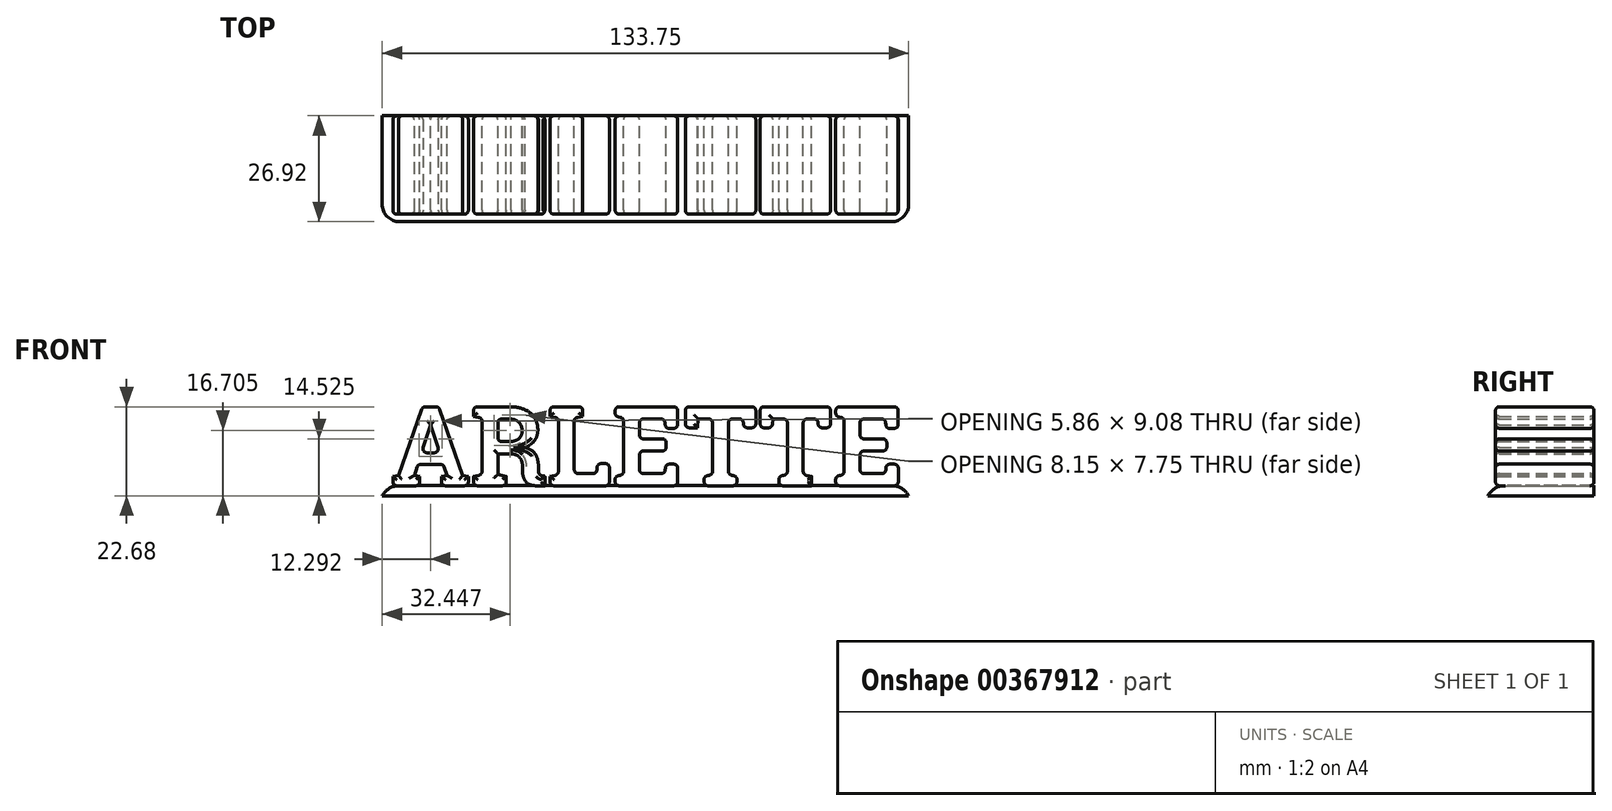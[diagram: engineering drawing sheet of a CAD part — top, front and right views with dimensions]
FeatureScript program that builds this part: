
annotation { "Feature Type Name" : "Feature", "Feature Type Description" : "" }
export const myFeature = defineFeature(function(context is Context, id is Id, definition is map)
    precondition{}
    {
        {
            var Q0;
            Q0=qCreatedBy(makeId("Front.planeOp"),FACE);
            var sketch = newSketch(context, id + "F0", { "sketchPlane" : qUnion([Q0])});
            skText(sketch, "E0", { "text": "ARLETTE", "fontName": "RobotoSlab-Bold.ttf"});
            const initialGuessF0  = {"E0": [-0.06833, 0.0026, 1, 0, 0.02034]};
            skSetInitialGuess(sketch, initialGuessF0);
            skSolve(sketch);
        }
        {
            var Q0;
            Q0 = qSketchRegion(id + "F0", true);
            extrude(context, id + "F1", {"entities" : qUnion([Q0]), "depth" : 25 * mm});
        }
        {
            var Q0;
            Q0=makeQuery(id+"F1.opExtrude","CAP_FACE",FACE,{"disambiguationData":[OSD([sQuery(id+"F0.wireOp",EDGE,"E0.sketch_text.stroke-0"),sQuery(id+"F0.wireOp",EDGE,"E0.sketch_text.stroke-1"),sQuery(id+"F0.wireOp",EDGE,"E0.sketch_text.stroke-2"),sQuery(id+"F0.wireOp",EDGE,"E0.sketch_text.stroke-3"),sQuery(id+"F0.wireOp",EDGE,"E0.sketch_text.stroke-4"),sQuery(id+"F0.wireOp",EDGE,"E0.sketch_text.stroke-5"),sQuery(id+"F0.wireOp",EDGE,"E0.sketch_text.stroke-6"),sQuery(id+"F0.wireOp",EDGE,"E0.sketch_text.stroke-7"),sQuery(id+"F0.wireOp",EDGE,"E0.sketch_text.stroke-8"),sQuery(id+"F0.wireOp",EDGE,"E0.sketch_text.stroke-9"),sQuery(id+"F0.wireOp",EDGE,"E0.sketch_text.stroke-10"),sQuery(id+"F0.wireOp",EDGE,"E0.sketch_text.stroke-11"),sQuery(id+"F0.wireOp",EDGE,"E0.sketch_text.stroke-12"),sQuery(id+"F0.wireOp",EDGE,"E0.sketch_text.stroke-13"),sQuery(id+"F0.wireOp",EDGE,"E0.sketch_text.stroke-14"),sQuery(id+"F0.wireOp",EDGE,"E0.sketch_text.stroke-15"),sQuery(id+"F0.wireOp",EDGE,"E0.sketch_text.stroke-16"),sQuery(id+"F0.wireOp",EDGE,"E0.sketch_text.stroke-17"),sQuery(id+"F0.wireOp",EDGE,"E0.sketch_text.stroke-18"),sQuery(id+"F0.wireOp",EDGE,"E0.sketch_text.stroke-19")])],"isStart":false});
            var Q1;
            Q1=makeQuery(id+"F1.opExtrude","CAP_FACE",FACE,{"disambiguationData":[OSD([sQuery(id+"F0.wireOp",EDGE,"E0.sketch_text.stroke-20"),sQuery(id+"F0.wireOp",EDGE,"E0.sketch_text.stroke-21"),sQuery(id+"F0.wireOp",EDGE,"E0.sketch_text.stroke-22"),sQuery(id+"F0.wireOp",EDGE,"E0.sketch_text.stroke-23"),sQuery(id+"F0.wireOp",EDGE,"E0.sketch_text.stroke-24"),sQuery(id+"F0.wireOp",EDGE,"E0.sketch_text.stroke-25"),sQuery(id+"F0.wireOp",EDGE,"E0.sketch_text.stroke-26"),sQuery(id+"F0.wireOp",EDGE,"E0.sketch_text.stroke-27"),sQuery(id+"F0.wireOp",EDGE,"E0.sketch_text.stroke-28"),sQuery(id+"F0.wireOp",EDGE,"E0.sketch_text.stroke-29"),sQuery(id+"F0.wireOp",EDGE,"E0.sketch_text.stroke-30"),sQuery(id+"F0.wireOp",EDGE,"E0.sketch_text.stroke-31"),sQuery(id+"F0.wireOp",EDGE,"E0.sketch_text.stroke-32"),sQuery(id+"F0.wireOp",EDGE,"E0.sketch_text.stroke-33"),sQuery(id+"F0.wireOp",EDGE,"E0.sketch_text.stroke-34"),sQuery(id+"F0.wireOp",EDGE,"E0.sketch_text.stroke-35"),sQuery(id+"F0.wireOp",EDGE,"E0.sketch_text.stroke-36"),sQuery(id+"F0.wireOp",EDGE,"E0.sketch_text.stroke-37"),sQuery(id+"F0.wireOp",EDGE,"E0.sketch_text.stroke-38"),sQuery(id+"F0.wireOp",EDGE,"E0.sketch_text.stroke-39"),sQuery(id+"F0.wireOp",EDGE,"E0.sketch_text.stroke-40"),sQuery(id+"F0.wireOp",EDGE,"E0.sketch_text.stroke-41"),sQuery(id+"F0.wireOp",EDGE,"E0.sketch_text.stroke-42"),sQuery(id+"F0.wireOp",EDGE,"E0.sketch_text.stroke-43"),sQuery(id+"F0.wireOp",EDGE,"E0.sketch_text.stroke-44"),sQuery(id+"F0.wireOp",EDGE,"E0.sketch_text.stroke-45"),sQuery(id+"F0.wireOp",EDGE,"E0.sketch_text.stroke-46"),sQuery(id+"F0.wireOp",EDGE,"E0.sketch_text.stroke-47"),sQuery(id+"F0.wireOp",EDGE,"E0.sketch_text.stroke-48"),sQuery(id+"F0.wireOp",EDGE,"E0.sketch_text.stroke-49"),sQuery(id+"F0.wireOp",EDGE,"E0.sketch_text.stroke-50"),sQuery(id+"F0.wireOp",EDGE,"E0.sketch_text.stroke-51"),sQuery(id+"F0.wireOp",EDGE,"E0.sketch_text.stroke-52"),sQuery(id+"F0.wireOp",EDGE,"E0.sketch_text.stroke-53"),sQuery(id+"F0.wireOp",EDGE,"E0.sketch_text.stroke-54"),sQuery(id+"F0.wireOp",EDGE,"E0.sketch_text.stroke-55")])],"isStart":false});
            var Q2;
            Q2=makeQuery(id+"F1.opExtrude","CAP_FACE",FACE,{"disambiguationData":[OSD([sQuery(id+"F0.wireOp",EDGE,"E0.sketch_text.stroke-56"),sQuery(id+"F0.wireOp",EDGE,"E0.sketch_text.stroke-57"),sQuery(id+"F0.wireOp",EDGE,"E0.sketch_text.stroke-58"),sQuery(id+"F0.wireOp",EDGE,"E0.sketch_text.stroke-59"),sQuery(id+"F0.wireOp",EDGE,"E0.sketch_text.stroke-60"),sQuery(id+"F0.wireOp",EDGE,"E0.sketch_text.stroke-61"),sQuery(id+"F0.wireOp",EDGE,"E0.sketch_text.stroke-62"),sQuery(id+"F0.wireOp",EDGE,"E0.sketch_text.stroke-63"),sQuery(id+"F0.wireOp",EDGE,"E0.sketch_text.stroke-64"),sQuery(id+"F0.wireOp",EDGE,"E0.sketch_text.stroke-65"),sQuery(id+"F0.wireOp",EDGE,"E0.sketch_text.stroke-66"),sQuery(id+"F0.wireOp",EDGE,"E0.sketch_text.stroke-67"),sQuery(id+"F0.wireOp",EDGE,"E0.sketch_text.stroke-68"),sQuery(id+"F0.wireOp",EDGE,"E0.sketch_text.stroke-69"),sQuery(id+"F0.wireOp",EDGE,"E0.sketch_text.stroke-70"),sQuery(id+"F0.wireOp",EDGE,"E0.sketch_text.stroke-71")])],"isStart":false});
            var Q3;
            Q3=makeQuery(id+"F1.opExtrude","CAP_FACE",FACE,{"disambiguationData":[OSD([sQuery(id+"F0.wireOp",EDGE,"E0.sketch_text.stroke-72"),sQuery(id+"F0.wireOp",EDGE,"E0.sketch_text.stroke-73"),sQuery(id+"F0.wireOp",EDGE,"E0.sketch_text.stroke-74"),sQuery(id+"F0.wireOp",EDGE,"E0.sketch_text.stroke-75"),sQuery(id+"F0.wireOp",EDGE,"E0.sketch_text.stroke-76"),sQuery(id+"F0.wireOp",EDGE,"E0.sketch_text.stroke-77"),sQuery(id+"F0.wireOp",EDGE,"E0.sketch_text.stroke-78"),sQuery(id+"F0.wireOp",EDGE,"E0.sketch_text.stroke-79"),sQuery(id+"F0.wireOp",EDGE,"E0.sketch_text.stroke-80"),sQuery(id+"F0.wireOp",EDGE,"E0.sketch_text.stroke-81"),sQuery(id+"F0.wireOp",EDGE,"E0.sketch_text.stroke-82"),sQuery(id+"F0.wireOp",EDGE,"E0.sketch_text.stroke-83"),sQuery(id+"F0.wireOp",EDGE,"E0.sketch_text.stroke-84"),sQuery(id+"F0.wireOp",EDGE,"E0.sketch_text.stroke-85"),sQuery(id+"F0.wireOp",EDGE,"E0.sketch_text.stroke-86"),sQuery(id+"F0.wireOp",EDGE,"E0.sketch_text.stroke-87"),sQuery(id+"F0.wireOp",EDGE,"E0.sketch_text.stroke-88"),sQuery(id+"F0.wireOp",EDGE,"E0.sketch_text.stroke-89"),sQuery(id+"F0.wireOp",EDGE,"E0.sketch_text.stroke-90"),sQuery(id+"F0.wireOp",EDGE,"E0.sketch_text.stroke-91"),sQuery(id+"F0.wireOp",EDGE,"E0.sketch_text.stroke-92")])],"isStart":false});
            var Q4;
            Q4=makeQuery(id+"F1.opExtrude","CAP_FACE",FACE,{"disambiguationData":[OSD([sQuery(id+"F0.wireOp",EDGE,"E0.sketch_text.stroke-93"),sQuery(id+"F0.wireOp",EDGE,"E0.sketch_text.stroke-94"),sQuery(id+"F0.wireOp",EDGE,"E0.sketch_text.stroke-95"),sQuery(id+"F0.wireOp",EDGE,"E0.sketch_text.stroke-96"),sQuery(id+"F0.wireOp",EDGE,"E0.sketch_text.stroke-97"),sQuery(id+"F0.wireOp",EDGE,"E0.sketch_text.stroke-98"),sQuery(id+"F0.wireOp",EDGE,"E0.sketch_text.stroke-99"),sQuery(id+"F0.wireOp",EDGE,"E0.sketch_text.stroke-100"),sQuery(id+"F0.wireOp",EDGE,"E0.sketch_text.stroke-101"),sQuery(id+"F0.wireOp",EDGE,"E0.sketch_text.stroke-102"),sQuery(id+"F0.wireOp",EDGE,"E0.sketch_text.stroke-103"),sQuery(id+"F0.wireOp",EDGE,"E0.sketch_text.stroke-104"),sQuery(id+"F0.wireOp",EDGE,"E0.sketch_text.stroke-105"),sQuery(id+"F0.wireOp",EDGE,"E0.sketch_text.stroke-106"),sQuery(id+"F0.wireOp",EDGE,"E0.sketch_text.stroke-107"),sQuery(id+"F0.wireOp",EDGE,"E0.sketch_text.stroke-108")])],"isStart":false});
            var Q5;
            Q5=makeQuery(id+"F1.opExtrude","CAP_FACE",FACE,{"disambiguationData":[OSD([sQuery(id+"F0.wireOp",EDGE,"E0.sketch_text.stroke-109"),sQuery(id+"F0.wireOp",EDGE,"E0.sketch_text.stroke-110"),sQuery(id+"F0.wireOp",EDGE,"E0.sketch_text.stroke-111"),sQuery(id+"F0.wireOp",EDGE,"E0.sketch_text.stroke-112"),sQuery(id+"F0.wireOp",EDGE,"E0.sketch_text.stroke-113"),sQuery(id+"F0.wireOp",EDGE,"E0.sketch_text.stroke-114"),sQuery(id+"F0.wireOp",EDGE,"E0.sketch_text.stroke-115"),sQuery(id+"F0.wireOp",EDGE,"E0.sketch_text.stroke-116"),sQuery(id+"F0.wireOp",EDGE,"E0.sketch_text.stroke-117"),sQuery(id+"F0.wireOp",EDGE,"E0.sketch_text.stroke-118"),sQuery(id+"F0.wireOp",EDGE,"E0.sketch_text.stroke-119"),sQuery(id+"F0.wireOp",EDGE,"E0.sketch_text.stroke-120"),sQuery(id+"F0.wireOp",EDGE,"E0.sketch_text.stroke-121"),sQuery(id+"F0.wireOp",EDGE,"E0.sketch_text.stroke-122"),sQuery(id+"F0.wireOp",EDGE,"E0.sketch_text.stroke-123"),sQuery(id+"F0.wireOp",EDGE,"E0.sketch_text.stroke-124")])],"isStart":false});
            var Q6;
            Q6=makeQuery(id+"F1.opExtrude","CAP_FACE",FACE,{"disambiguationData":[OSD([sQuery(id+"F0.wireOp",EDGE,"E0.sketch_text.stroke-125"),sQuery(id+"F0.wireOp",EDGE,"E0.sketch_text.stroke-126"),sQuery(id+"F0.wireOp",EDGE,"E0.sketch_text.stroke-127"),sQuery(id+"F0.wireOp",EDGE,"E0.sketch_text.stroke-128"),sQuery(id+"F0.wireOp",EDGE,"E0.sketch_text.stroke-129"),sQuery(id+"F0.wireOp",EDGE,"E0.sketch_text.stroke-130"),sQuery(id+"F0.wireOp",EDGE,"E0.sketch_text.stroke-131"),sQuery(id+"F0.wireOp",EDGE,"E0.sketch_text.stroke-132"),sQuery(id+"F0.wireOp",EDGE,"E0.sketch_text.stroke-133"),sQuery(id+"F0.wireOp",EDGE,"E0.sketch_text.stroke-134"),sQuery(id+"F0.wireOp",EDGE,"E0.sketch_text.stroke-135"),sQuery(id+"F0.wireOp",EDGE,"E0.sketch_text.stroke-136"),sQuery(id+"F0.wireOp",EDGE,"E0.sketch_text.stroke-137"),sQuery(id+"F0.wireOp",EDGE,"E0.sketch_text.stroke-138"),sQuery(id+"F0.wireOp",EDGE,"E0.sketch_text.stroke-139"),sQuery(id+"F0.wireOp",EDGE,"E0.sketch_text.stroke-140"),sQuery(id+"F0.wireOp",EDGE,"E0.sketch_text.stroke-141"),sQuery(id+"F0.wireOp",EDGE,"E0.sketch_text.stroke-142"),sQuery(id+"F0.wireOp",EDGE,"E0.sketch_text.stroke-143"),sQuery(id+"F0.wireOp",EDGE,"E0.sketch_text.stroke-144"),sQuery(id+"F0.wireOp",EDGE,"E0.sketch_text.stroke-145")])],"isStart":false});
            var Q7;
            Q7=makeQuery(id+"F1.opExtrude","SWEPT_EDGE",EDGE,{"disambiguationData":[OSD([sQuery(id+"F0.wireOp",EDGE,"E0.sketch_text.stroke-14"),sQuery(id+"F0.wireOp",EDGE,"E0.sketch_text.stroke-15")])]});
            var Q8;
            Q8=makeQuery(id+"F1.opExtrude","SWEPT_EDGE",EDGE,{"disambiguationData":[OSD([sQuery(id+"F0.wireOp",EDGE,"E0.sketch_text.stroke-2"),sQuery(id+"F0.wireOp",EDGE,"E0.sketch_text.stroke-3")])]});
            var Q9;
            Q9=makeQuery(id+"F1.opExtrude","SWEPT_EDGE",EDGE,{"disambiguationData":[OSD([sQuery(id+"F0.wireOp",EDGE,"E0.sketch_text.stroke-1"),sQuery(id+"F0.wireOp",EDGE,"E0.sketch_text.stroke-2")])]});
            var Q10;
            Q10=makeQuery(id+"F1.opExtrude","CAP_FACE",FACE,{"disambiguationData":[OSD([sQuery(id+"F0.wireOp",EDGE,"E0.sketch_text.stroke-0"),sQuery(id+"F0.wireOp",EDGE,"E0.sketch_text.stroke-1"),sQuery(id+"F0.wireOp",EDGE,"E0.sketch_text.stroke-2"),sQuery(id+"F0.wireOp",EDGE,"E0.sketch_text.stroke-3"),sQuery(id+"F0.wireOp",EDGE,"E0.sketch_text.stroke-4"),sQuery(id+"F0.wireOp",EDGE,"E0.sketch_text.stroke-5"),sQuery(id+"F0.wireOp",EDGE,"E0.sketch_text.stroke-6"),sQuery(id+"F0.wireOp",EDGE,"E0.sketch_text.stroke-7"),sQuery(id+"F0.wireOp",EDGE,"E0.sketch_text.stroke-8"),sQuery(id+"F0.wireOp",EDGE,"E0.sketch_text.stroke-9"),sQuery(id+"F0.wireOp",EDGE,"E0.sketch_text.stroke-10"),sQuery(id+"F0.wireOp",EDGE,"E0.sketch_text.stroke-11"),sQuery(id+"F0.wireOp",EDGE,"E0.sketch_text.stroke-12"),sQuery(id+"F0.wireOp",EDGE,"E0.sketch_text.stroke-13"),sQuery(id+"F0.wireOp",EDGE,"E0.sketch_text.stroke-14"),sQuery(id+"F0.wireOp",EDGE,"E0.sketch_text.stroke-15"),sQuery(id+"F0.wireOp",EDGE,"E0.sketch_text.stroke-16"),sQuery(id+"F0.wireOp",EDGE,"E0.sketch_text.stroke-17"),sQuery(id+"F0.wireOp",EDGE,"E0.sketch_text.stroke-18"),sQuery(id+"F0.wireOp",EDGE,"E0.sketch_text.stroke-19")])],"isStart":true});
            var Q11;
            Q11=makeQuery(id+"F1.opExtrude","SWEPT_FACE",FACE,{"disambiguationData":[OSD([sQuery(id+"F0.wireOp",EDGE,"E0.sketch_text.stroke-14")])]});
            var Q12;
            Q12=makeQuery(id+"F1.opExtrude","SWEPT_FACE",FACE,{"disambiguationData":[OSD([sQuery(id+"F0.wireOp",EDGE,"E0.sketch_text.stroke-6")])]});
            var Q13;
            Q13=makeQuery(id+"F1.opExtrude","SWEPT_FACE",FACE,{"disambiguationData":[OSD([sQuery(id+"F0.wireOp",EDGE,"E0.sketch_text.stroke-10")])]});
            var Q14;
            Q14=makeQuery(id+"F1.opExtrude","SWEPT_FACE",FACE,{"disambiguationData":[OSD([sQuery(id+"F0.wireOp",EDGE,"E0.sketch_text.stroke-16")])]});
            var Q15;
            Q15=makeQuery(id+"F1.opExtrude","SWEPT_FACE",FACE,{"disambiguationData":[OSD([sQuery(id+"F0.wireOp",EDGE,"E0.sketch_text.stroke-44")])]});
            var Q16;
            Q16=makeQuery(id+"F1.opExtrude","SWEPT_FACE",FACE,{"disambiguationData":[OSD([sQuery(id+"F0.wireOp",EDGE,"E0.sketch_text.stroke-47"),sQuery(id+"F0.wireOp",EDGE,"E0.sketch_text.stroke-48")])]});
            var Q17;
            Q17=makeQuery(id+"F1.opExtrude","SWEPT_FACE",FACE,{"disambiguationData":[OSD([sQuery(id+"F0.wireOp",EDGE,"E0.sketch_text.stroke-41")])]});
            var Q18;
            Q18=makeQuery(id+"F1.opExtrude","SWEPT_FACE",FACE,{"disambiguationData":[OSD([sQuery(id+"F0.wireOp",EDGE,"E0.sketch_text.stroke-55")])]});
            var Q19;
            Q19=makeQuery(id+"F1.opExtrude","CAP_FACE",FACE,{"disambiguationData":[OSD([sQuery(id+"F0.wireOp",EDGE,"E0.sketch_text.stroke-20"),sQuery(id+"F0.wireOp",EDGE,"E0.sketch_text.stroke-21"),sQuery(id+"F0.wireOp",EDGE,"E0.sketch_text.stroke-22"),sQuery(id+"F0.wireOp",EDGE,"E0.sketch_text.stroke-23"),sQuery(id+"F0.wireOp",EDGE,"E0.sketch_text.stroke-24"),sQuery(id+"F0.wireOp",EDGE,"E0.sketch_text.stroke-25"),sQuery(id+"F0.wireOp",EDGE,"E0.sketch_text.stroke-26"),sQuery(id+"F0.wireOp",EDGE,"E0.sketch_text.stroke-27"),sQuery(id+"F0.wireOp",EDGE,"E0.sketch_text.stroke-28"),sQuery(id+"F0.wireOp",EDGE,"E0.sketch_text.stroke-29"),sQuery(id+"F0.wireOp",EDGE,"E0.sketch_text.stroke-30"),sQuery(id+"F0.wireOp",EDGE,"E0.sketch_text.stroke-31"),sQuery(id+"F0.wireOp",EDGE,"E0.sketch_text.stroke-32"),sQuery(id+"F0.wireOp",EDGE,"E0.sketch_text.stroke-33"),sQuery(id+"F0.wireOp",EDGE,"E0.sketch_text.stroke-34"),sQuery(id+"F0.wireOp",EDGE,"E0.sketch_text.stroke-35"),sQuery(id+"F0.wireOp",EDGE,"E0.sketch_text.stroke-36"),sQuery(id+"F0.wireOp",EDGE,"E0.sketch_text.stroke-37"),sQuery(id+"F0.wireOp",EDGE,"E0.sketch_text.stroke-38"),sQuery(id+"F0.wireOp",EDGE,"E0.sketch_text.stroke-39"),sQuery(id+"F0.wireOp",EDGE,"E0.sketch_text.stroke-40"),sQuery(id+"F0.wireOp",EDGE,"E0.sketch_text.stroke-41"),sQuery(id+"F0.wireOp",EDGE,"E0.sketch_text.stroke-42"),sQuery(id+"F0.wireOp",EDGE,"E0.sketch_text.stroke-43"),sQuery(id+"F0.wireOp",EDGE,"E0.sketch_text.stroke-44"),sQuery(id+"F0.wireOp",EDGE,"E0.sketch_text.stroke-45"),sQuery(id+"F0.wireOp",EDGE,"E0.sketch_text.stroke-46"),sQuery(id+"F0.wireOp",EDGE,"E0.sketch_text.stroke-47"),sQuery(id+"F0.wireOp",EDGE,"E0.sketch_text.stroke-48"),sQuery(id+"F0.wireOp",EDGE,"E0.sketch_text.stroke-49"),sQuery(id+"F0.wireOp",EDGE,"E0.sketch_text.stroke-50"),sQuery(id+"F0.wireOp",EDGE,"E0.sketch_text.stroke-51"),sQuery(id+"F0.wireOp",EDGE,"E0.sketch_text.stroke-52"),sQuery(id+"F0.wireOp",EDGE,"E0.sketch_text.stroke-53"),sQuery(id+"F0.wireOp",EDGE,"E0.sketch_text.stroke-54"),sQuery(id+"F0.wireOp",EDGE,"E0.sketch_text.stroke-55")])],"isStart":true});
            var Q20;
            Q20=makeQuery(id+"F1.opExtrude","CAP_FACE",FACE,{"disambiguationData":[OSD([sQuery(id+"F0.wireOp",EDGE,"E0.sketch_text.stroke-56"),sQuery(id+"F0.wireOp",EDGE,"E0.sketch_text.stroke-57"),sQuery(id+"F0.wireOp",EDGE,"E0.sketch_text.stroke-58"),sQuery(id+"F0.wireOp",EDGE,"E0.sketch_text.stroke-59"),sQuery(id+"F0.wireOp",EDGE,"E0.sketch_text.stroke-60"),sQuery(id+"F0.wireOp",EDGE,"E0.sketch_text.stroke-61"),sQuery(id+"F0.wireOp",EDGE,"E0.sketch_text.stroke-62"),sQuery(id+"F0.wireOp",EDGE,"E0.sketch_text.stroke-63"),sQuery(id+"F0.wireOp",EDGE,"E0.sketch_text.stroke-64"),sQuery(id+"F0.wireOp",EDGE,"E0.sketch_text.stroke-65"),sQuery(id+"F0.wireOp",EDGE,"E0.sketch_text.stroke-66"),sQuery(id+"F0.wireOp",EDGE,"E0.sketch_text.stroke-67"),sQuery(id+"F0.wireOp",EDGE,"E0.sketch_text.stroke-68"),sQuery(id+"F0.wireOp",EDGE,"E0.sketch_text.stroke-69"),sQuery(id+"F0.wireOp",EDGE,"E0.sketch_text.stroke-70"),sQuery(id+"F0.wireOp",EDGE,"E0.sketch_text.stroke-71")])],"isStart":true});
            var Q21;
            Q21=makeQuery(id+"F1.opExtrude","SWEPT_FACE",FACE,{"disambiguationData":[OSD([sQuery(id+"F0.wireOp",EDGE,"E0.sketch_text.stroke-58")])]});
            var Q22;
            Q22=makeQuery(id+"F1.opExtrude","SWEPT_FACE",FACE,{"disambiguationData":[OSD([sQuery(id+"F0.wireOp",EDGE,"E0.sketch_text.stroke-61"),sQuery(id+"F0.wireOp",EDGE,"E0.sketch_text.stroke-62"),sQuery(id+"F0.wireOp",EDGE,"E0.sketch_text.stroke-63")])]});
            var Q23;
            Q23=makeQuery(id+"F1.opExtrude","SWEPT_FACE",FACE,{"disambiguationData":[OSD([sQuery(id+"F0.wireOp",EDGE,"E0.sketch_text.stroke-66")])]});
            var Q24;
            Q24=makeQuery(id+"F1.opExtrude","SWEPT_FACE",FACE,{"disambiguationData":[OSD([sQuery(id+"F0.wireOp",EDGE,"E0.sketch_text.stroke-71")])]});
            var Q25;
            Q25=makeQuery(id+"F1.opExtrude","SWEPT_FACE",FACE,{"disambiguationData":[OSD([sQuery(id+"F0.wireOp",EDGE,"E0.sketch_text.stroke-67")])]});
            var Q26;
            Q26=makeQuery(id+"F1.opExtrude","SWEPT_FACE",FACE,{"disambiguationData":[OSD([sQuery(id+"F0.wireOp",EDGE,"E0.sketch_text.stroke-69")])]});
            var Q27;
            Q27=makeQuery(id+"F1.opExtrude","SWEPT_FACE",FACE,{"disambiguationData":[OSD([sQuery(id+"F0.wireOp",EDGE,"E0.sketch_text.stroke-70")])]});
            var Q28;
            Q28=makeQuery(id+"F1.opExtrude","CAP_FACE",FACE,{"disambiguationData":[OSD([sQuery(id+"F0.wireOp",EDGE,"E0.sketch_text.stroke-72"),sQuery(id+"F0.wireOp",EDGE,"E0.sketch_text.stroke-73"),sQuery(id+"F0.wireOp",EDGE,"E0.sketch_text.stroke-74"),sQuery(id+"F0.wireOp",EDGE,"E0.sketch_text.stroke-75"),sQuery(id+"F0.wireOp",EDGE,"E0.sketch_text.stroke-76"),sQuery(id+"F0.wireOp",EDGE,"E0.sketch_text.stroke-77"),sQuery(id+"F0.wireOp",EDGE,"E0.sketch_text.stroke-78"),sQuery(id+"F0.wireOp",EDGE,"E0.sketch_text.stroke-79"),sQuery(id+"F0.wireOp",EDGE,"E0.sketch_text.stroke-80"),sQuery(id+"F0.wireOp",EDGE,"E0.sketch_text.stroke-81"),sQuery(id+"F0.wireOp",EDGE,"E0.sketch_text.stroke-82"),sQuery(id+"F0.wireOp",EDGE,"E0.sketch_text.stroke-83"),sQuery(id+"F0.wireOp",EDGE,"E0.sketch_text.stroke-84"),sQuery(id+"F0.wireOp",EDGE,"E0.sketch_text.stroke-85"),sQuery(id+"F0.wireOp",EDGE,"E0.sketch_text.stroke-86"),sQuery(id+"F0.wireOp",EDGE,"E0.sketch_text.stroke-87"),sQuery(id+"F0.wireOp",EDGE,"E0.sketch_text.stroke-88"),sQuery(id+"F0.wireOp",EDGE,"E0.sketch_text.stroke-89"),sQuery(id+"F0.wireOp",EDGE,"E0.sketch_text.stroke-90"),sQuery(id+"F0.wireOp",EDGE,"E0.sketch_text.stroke-91"),sQuery(id+"F0.wireOp",EDGE,"E0.sketch_text.stroke-92")])],"isStart":true});
            var Q29;
            Q29=makeQuery(id+"F1.opExtrude","SWEPT_FACE",FACE,{"disambiguationData":[OSD([sQuery(id+"F0.wireOp",EDGE,"E0.sketch_text.stroke-81")])]});
            var Q30;
            Q30=makeQuery(id+"F1.opExtrude","SWEPT_FACE",FACE,{"disambiguationData":[OSD([sQuery(id+"F0.wireOp",EDGE,"E0.sketch_text.stroke-79")])]});
            var Q31;
            Q31=makeQuery(id+"F1.opExtrude","SWEPT_FACE",FACE,{"disambiguationData":[OSD([sQuery(id+"F0.wireOp",EDGE,"E0.sketch_text.stroke-83")])]});
            var Q32;
            Q32=makeQuery(id+"F1.opExtrude","SWEPT_FACE",FACE,{"disambiguationData":[OSD([sQuery(id+"F0.wireOp",EDGE,"E0.sketch_text.stroke-84"),sQuery(id+"F0.wireOp",EDGE,"E0.sketch_text.stroke-85")])]});
            var Q33;
            Q33=makeQuery(id+"F1.opExtrude","SWEPT_FACE",FACE,{"disambiguationData":[OSD([sQuery(id+"F0.wireOp",EDGE,"E0.sketch_text.stroke-86")])]});
            var Q34;
            Q34=makeQuery(id+"F1.opExtrude","SWEPT_FACE",FACE,{"disambiguationData":[OSD([sQuery(id+"F0.wireOp",EDGE,"E0.sketch_text.stroke-90")])]});
            var Q35;
            Q35=makeQuery(id+"F1.opExtrude","SWEPT_FACE",FACE,{"disambiguationData":[OSD([sQuery(id+"F0.wireOp",EDGE,"E0.sketch_text.stroke-89")])]});
            var Q36;
            Q36=makeQuery(id+"F1.opExtrude","SWEPT_EDGE",EDGE,{"disambiguationData":[OSD([sQuery(id+"F0.wireOp",EDGE,"E0.sketch_text.stroke-87"),sQuery(id+"F0.wireOp",EDGE,"E0.sketch_text.stroke-88")])]});
            var Q37;
            Q37=makeQuery(id+"F1.opExtrude","SWEPT_FACE",FACE,{"disambiguationData":[OSD([sQuery(id+"F0.wireOp",EDGE,"E0.sketch_text.stroke-91")])]});
            var Q38;
            Q38=makeQuery(id+"F1.opExtrude","SWEPT_FACE",FACE,{"disambiguationData":[OSD([sQuery(id+"F0.wireOp",EDGE,"E0.sketch_text.stroke-92")])]});
            var Q39;
            Q39=makeQuery(id+"F1.opExtrude","SWEPT_FACE",FACE,{"disambiguationData":[OSD([sQuery(id+"F0.wireOp",EDGE,"E0.sketch_text.stroke-72")])]});
            var Q40;
            Q40=makeQuery(id+"F1.opExtrude","SWEPT_FACE",FACE,{"disambiguationData":[OSD([sQuery(id+"F0.wireOp",EDGE,"E0.sketch_text.stroke-73")])]});
            var Q41;
            Q41=makeQuery(id+"F1.opExtrude","SWEPT_FACE",FACE,{"disambiguationData":[OSD([sQuery(id+"F0.wireOp",EDGE,"E0.sketch_text.stroke-74")])]});
            var Q42;
            Q42=makeQuery(id+"F1.opExtrude","SWEPT_FACE",FACE,{"disambiguationData":[OSD([sQuery(id+"F0.wireOp",EDGE,"E0.sketch_text.stroke-76")])]});
            var Q43;
            Q43=makeQuery(id+"F1.opExtrude","CAP_FACE",FACE,{"disambiguationData":[OSD([sQuery(id+"F0.wireOp",EDGE,"E0.sketch_text.stroke-93"),sQuery(id+"F0.wireOp",EDGE,"E0.sketch_text.stroke-94"),sQuery(id+"F0.wireOp",EDGE,"E0.sketch_text.stroke-95"),sQuery(id+"F0.wireOp",EDGE,"E0.sketch_text.stroke-96"),sQuery(id+"F0.wireOp",EDGE,"E0.sketch_text.stroke-97"),sQuery(id+"F0.wireOp",EDGE,"E0.sketch_text.stroke-98"),sQuery(id+"F0.wireOp",EDGE,"E0.sketch_text.stroke-99"),sQuery(id+"F0.wireOp",EDGE,"E0.sketch_text.stroke-100"),sQuery(id+"F0.wireOp",EDGE,"E0.sketch_text.stroke-101"),sQuery(id+"F0.wireOp",EDGE,"E0.sketch_text.stroke-102"),sQuery(id+"F0.wireOp",EDGE,"E0.sketch_text.stroke-103"),sQuery(id+"F0.wireOp",EDGE,"E0.sketch_text.stroke-104"),sQuery(id+"F0.wireOp",EDGE,"E0.sketch_text.stroke-105"),sQuery(id+"F0.wireOp",EDGE,"E0.sketch_text.stroke-106"),sQuery(id+"F0.wireOp",EDGE,"E0.sketch_text.stroke-107"),sQuery(id+"F0.wireOp",EDGE,"E0.sketch_text.stroke-108")])],"isStart":true});
            var Q44;
            Q44=makeQuery(id+"F1.opExtrude","SWEPT_FACE",FACE,{"disambiguationData":[OSD([sQuery(id+"F0.wireOp",EDGE,"E0.sketch_text.stroke-108")])]});
            var Q45;
            Q45=makeQuery(id+"F1.opExtrude","SWEPT_FACE",FACE,{"disambiguationData":[OSD([sQuery(id+"F0.wireOp",EDGE,"E0.sketch_text.stroke-107")])]});
            var Q46;
            Q46=makeQuery(id+"F1.opExtrude","SWEPT_FACE",FACE,{"disambiguationData":[OSD([sQuery(id+"F0.wireOp",EDGE,"E0.sketch_text.stroke-103")])]});
            var Q47;
            Q47=makeQuery(id+"F1.opExtrude","SWEPT_FACE",FACE,{"disambiguationData":[OSD([sQuery(id+"F0.wireOp",EDGE,"E0.sketch_text.stroke-101")])]});
            var Q48;
            Q48=makeQuery(id+"F1.opExtrude","SWEPT_FACE",FACE,{"disambiguationData":[OSD([sQuery(id+"F0.wireOp",EDGE,"E0.sketch_text.stroke-99")])]});
            var Q49;
            Q49=makeQuery(id+"F1.opExtrude","SWEPT_FACE",FACE,{"disambiguationData":[OSD([sQuery(id+"F0.wireOp",EDGE,"E0.sketch_text.stroke-97")])]});
            var Q50;
            Q50=makeQuery(id+"F1.opExtrude","SWEPT_FACE",FACE,{"disambiguationData":[OSD([sQuery(id+"F0.wireOp",EDGE,"E0.sketch_text.stroke-77")])]});
            var Q51;
            Q51=makeQuery(id+"F1.opExtrude","SWEPT_FACE",FACE,{"disambiguationData":[OSD([sQuery(id+"F0.wireOp",EDGE,"E0.sketch_text.stroke-96")])]});
            var Q52;
            Q52=makeQuery(id+"F1.opExtrude","SWEPT_FACE",FACE,{"disambiguationData":[OSD([sQuery(id+"F0.wireOp",EDGE,"E0.sketch_text.stroke-94")])]});
            var Q53;
            Q53=makeQuery(id+"F1.opExtrude","CAP_FACE",FACE,{"disambiguationData":[OSD([sQuery(id+"F0.wireOp",EDGE,"E0.sketch_text.stroke-109"),sQuery(id+"F0.wireOp",EDGE,"E0.sketch_text.stroke-110"),sQuery(id+"F0.wireOp",EDGE,"E0.sketch_text.stroke-111"),sQuery(id+"F0.wireOp",EDGE,"E0.sketch_text.stroke-112"),sQuery(id+"F0.wireOp",EDGE,"E0.sketch_text.stroke-113"),sQuery(id+"F0.wireOp",EDGE,"E0.sketch_text.stroke-114"),sQuery(id+"F0.wireOp",EDGE,"E0.sketch_text.stroke-115"),sQuery(id+"F0.wireOp",EDGE,"E0.sketch_text.stroke-116"),sQuery(id+"F0.wireOp",EDGE,"E0.sketch_text.stroke-117"),sQuery(id+"F0.wireOp",EDGE,"E0.sketch_text.stroke-118"),sQuery(id+"F0.wireOp",EDGE,"E0.sketch_text.stroke-119"),sQuery(id+"F0.wireOp",EDGE,"E0.sketch_text.stroke-120"),sQuery(id+"F0.wireOp",EDGE,"E0.sketch_text.stroke-121"),sQuery(id+"F0.wireOp",EDGE,"E0.sketch_text.stroke-122"),sQuery(id+"F0.wireOp",EDGE,"E0.sketch_text.stroke-123"),sQuery(id+"F0.wireOp",EDGE,"E0.sketch_text.stroke-124")])],"isStart":true});
            var Q54;
            Q54=makeQuery(id+"F1.opExtrude","SWEPT_FACE",FACE,{"disambiguationData":[OSD([sQuery(id+"F0.wireOp",EDGE,"E0.sketch_text.stroke-117")])]});
            var Q55;
            Q55=makeQuery(id+"F1.opExtrude","SWEPT_FACE",FACE,{"disambiguationData":[OSD([sQuery(id+"F0.wireOp",EDGE,"E0.sketch_text.stroke-119")])]});
            var Q56;
            Q56=makeQuery(id+"F1.opExtrude","SWEPT_FACE",FACE,{"disambiguationData":[OSD([sQuery(id+"F0.wireOp",EDGE,"E0.sketch_text.stroke-122")])]});
            var Q57;
            Q57=makeQuery(id+"F1.opExtrude","SWEPT_FACE",FACE,{"disambiguationData":[OSD([sQuery(id+"F0.wireOp",EDGE,"E0.sketch_text.stroke-124")])]});
            var Q58;
            Q58=makeQuery(id+"F1.opExtrude","SWEPT_FACE",FACE,{"disambiguationData":[OSD([sQuery(id+"F0.wireOp",EDGE,"E0.sketch_text.stroke-113")])]});
            var Q59;
            Q59=makeQuery(id+"F1.opExtrude","SWEPT_FACE",FACE,{"disambiguationData":[OSD([sQuery(id+"F0.wireOp",EDGE,"E0.sketch_text.stroke-110")])]});
            var Q60;
            Q60=makeQuery(id+"F1.opExtrude","SWEPT_FACE",FACE,{"disambiguationData":[OSD([sQuery(id+"F0.wireOp",EDGE,"E0.sketch_text.stroke-112")])]});
            var Q61;
            Q61=makeQuery(id+"F1.opExtrude","SWEPT_FACE",FACE,{"disambiguationData":[OSD([sQuery(id+"F0.wireOp",EDGE,"E0.sketch_text.stroke-136")])]});
            var Q62;
            Q62=makeQuery(id+"F1.opExtrude","SWEPT_FACE",FACE,{"disambiguationData":[OSD([sQuery(id+"F0.wireOp",EDGE,"E0.sketch_text.stroke-134")])]});
            var Q63;
            Q63=makeQuery(id+"F1.opExtrude","CAP_FACE",FACE,{"disambiguationData":[OSD([sQuery(id+"F0.wireOp",EDGE,"E0.sketch_text.stroke-125"),sQuery(id+"F0.wireOp",EDGE,"E0.sketch_text.stroke-126"),sQuery(id+"F0.wireOp",EDGE,"E0.sketch_text.stroke-127"),sQuery(id+"F0.wireOp",EDGE,"E0.sketch_text.stroke-128"),sQuery(id+"F0.wireOp",EDGE,"E0.sketch_text.stroke-129"),sQuery(id+"F0.wireOp",EDGE,"E0.sketch_text.stroke-130"),sQuery(id+"F0.wireOp",EDGE,"E0.sketch_text.stroke-131"),sQuery(id+"F0.wireOp",EDGE,"E0.sketch_text.stroke-132"),sQuery(id+"F0.wireOp",EDGE,"E0.sketch_text.stroke-133"),sQuery(id+"F0.wireOp",EDGE,"E0.sketch_text.stroke-134"),sQuery(id+"F0.wireOp",EDGE,"E0.sketch_text.stroke-135"),sQuery(id+"F0.wireOp",EDGE,"E0.sketch_text.stroke-136"),sQuery(id+"F0.wireOp",EDGE,"E0.sketch_text.stroke-137"),sQuery(id+"F0.wireOp",EDGE,"E0.sketch_text.stroke-138"),sQuery(id+"F0.wireOp",EDGE,"E0.sketch_text.stroke-139"),sQuery(id+"F0.wireOp",EDGE,"E0.sketch_text.stroke-140"),sQuery(id+"F0.wireOp",EDGE,"E0.sketch_text.stroke-141"),sQuery(id+"F0.wireOp",EDGE,"E0.sketch_text.stroke-142"),sQuery(id+"F0.wireOp",EDGE,"E0.sketch_text.stroke-143"),sQuery(id+"F0.wireOp",EDGE,"E0.sketch_text.stroke-144"),sQuery(id+"F0.wireOp",EDGE,"E0.sketch_text.stroke-145")])],"isStart":true});
            var Q64;
            Q64=makeQuery(id+"F1.opExtrude","SWEPT_FACE",FACE,{"disambiguationData":[OSD([sQuery(id+"F0.wireOp",EDGE,"E0.sketch_text.stroke-132")])]});
            var Q65;
            Q65=makeQuery(id+"F1.opExtrude","SWEPT_FACE",FACE,{"disambiguationData":[OSD([sQuery(id+"F0.wireOp",EDGE,"E0.sketch_text.stroke-128")])]});
            var Q66;
            Q66=makeQuery(id+"F1.opExtrude","SWEPT_FACE",FACE,{"disambiguationData":[OSD([sQuery(id+"F0.wireOp",EDGE,"E0.sketch_text.stroke-127")])]});
            var Q67;
            Q67=makeQuery(id+"F1.opExtrude","SWEPT_FACE",FACE,{"disambiguationData":[OSD([sQuery(id+"F0.wireOp",EDGE,"E0.sketch_text.stroke-125")])]});
            var Q68;
            Q68=makeQuery(id+"F1.opExtrude","SWEPT_FACE",FACE,{"disambiguationData":[OSD([sQuery(id+"F0.wireOp",EDGE,"E0.sketch_text.stroke-130")])]});
            var Q69;
            Q69=makeQuery(id+"F1.opExtrude","SWEPT_FACE",FACE,{"disambiguationData":[OSD([sQuery(id+"F0.wireOp",EDGE,"E0.sketch_text.stroke-144")])]});
            var Q70;
            Q70=makeQuery(id+"F1.opExtrude","SWEPT_FACE",FACE,{"disambiguationData":[OSD([sQuery(id+"F0.wireOp",EDGE,"E0.sketch_text.stroke-142")])]});
            var Q71;
            Q71=makeQuery(id+"F1.opExtrude","SWEPT_FACE",FACE,{"disambiguationData":[OSD([sQuery(id+"F0.wireOp",EDGE,"E0.sketch_text.stroke-137"),sQuery(id+"F0.wireOp",EDGE,"E0.sketch_text.stroke-138")])]});
            var Q72;
            Q72=makeQuery(id+"F1.opExtrude","SWEPT_FACE",FACE,{"disambiguationData":[OSD([sQuery(id+"F0.wireOp",EDGE,"E0.sketch_text.stroke-140")])]});
            fillet(context, id + "F2", {"entities" : qUnion([Q0, Q1, Q2, Q3, Q4, Q5, Q6, Q7, Q8, Q9, Q10, Q11, Q12, Q13, Q14, Q15, Q16, Q17, Q18, Q19, Q20, Q21, Q22, Q23, Q24, Q25, Q26, Q27, Q28, Q29, Q30, Q31, Q32, Q33, Q34, Q35, Q36, Q37, Q38, Q39, Q40, Q41, Q42, Q43, Q44, Q45, Q46, Q47, Q48, Q49, Q50, Q51, Q52, Q53, Q54, Q55, Q56, Q57, Q58, Q59, Q60, Q61, Q62, Q63, Q64, Q65, Q66, Q67, Q68, Q69, Q70, Q71, Q72]), "radius" : 1 * mm, "tangentPropagation" : true, "allowEdgeOverflow" : false});
        }
        {
            var Q0;
            Q0=qCreatedBy(makeId("Top.planeOp"),FACE);
            var sketch = newSketch(context, id + "F3", { "sketchPlane" : qUnion([Q0])});
            skLineSegment(sketch, "E1.bottom", {"start": v(-70.47, -26.92) * mm, "end": v(63.28, -26.92) * mm});
            skLineSegment(sketch, "E1.top", {"start": v(-70.47, 0) * mm, "end": v(63.28, 0) * mm});
            skLineSegment(sketch, "E1.left", {"start": v(-70.47, -26.92) * mm, "end": v(-70.47, 0) * mm});
            skLineSegment(sketch, "E1.right", {"start": v(63.28, -26.92) * mm, "end": v(63.28, 0) * mm});
            skSolve(sketch);
        }
        {
            var Q0;
            Q0=makeQuery(id+"F3.imprint","IMPRINT",FACE,{"disambiguationData":[TD([[makeQuery(id+"F3.imprint","IMPRINT",EDGE,{"derivedFrom":sQuery(id+"F3.wireOp",EDGE,"E1.bottom")}),1.0]])]});
            extrude(context, id + "F4", {"entities" : qUnion([Q0]), "depth" : 2.7 * mm});
        }
        {
            var Q0;
            Q0=makeQuery(id+"F4.opExtrude","CAP_EDGE",EDGE,{"disambiguationData":[OSD([sQuery(id+"F3.wireOp",EDGE,"E1.left")])],"isStart":false});
            var Q1;
            Q1=makeQuery(id+"F4.opExtrude","CAP_EDGE",EDGE,{"disambiguationData":[OSD([sQuery(id+"F3.wireOp",EDGE,"E1.bottom")])],"isStart":false});
            var Q2;
            Q2=makeQuery(id+"F4.opExtrude","CAP_EDGE",EDGE,{"disambiguationData":[OSD([sQuery(id+"F3.wireOp",EDGE,"E1.right")])],"isStart":false});
            fillet(context, id + "F5", {"entities" : qUnion([Q0, Q1, Q2]), "radius" : 5 * mm, "tangentPropagation" : true, "allowEdgeOverflow" : false});
        }
        {
            var Q0;
            Q0=makeQuery(id+"F5.opFillet","BLEND_EDGE",EDGE,{"blendedFrom":[makeQuery(id+"F4.opExtrude","CAP_EDGE",EDGE,{"disambiguationData":[OSD([sQuery(id+"F3.wireOp",EDGE,"E1.bottom")])],"isStart":false}),makeQuery(id+"F4.opExtrude","CAP_EDGE",EDGE,{"disambiguationData":[OSD([sQuery(id+"F3.wireOp",EDGE,"E1.left")])],"isStart":false})],"blendedInto":[]});
            var Q1;
            Q1=makeQuery(id+"F5.opFillet","BLEND_EDGE",EDGE,{"blendedFrom":[makeQuery(id+"F4.opExtrude","CAP_EDGE",EDGE,{"disambiguationData":[OSD([sQuery(id+"F3.wireOp",EDGE,"E1.bottom")])],"isStart":false}),makeQuery(id+"F4.opExtrude","CAP_EDGE",EDGE,{"disambiguationData":[OSD([sQuery(id+"F3.wireOp",EDGE,"E1.right")])],"isStart":false})],"blendedInto":[]});
            fillet(context, id + "F6", {"entities" : qUnion([Q0, Q1]), "radius" : 5 * mm, "tangentPropagation" : true, "allowEdgeOverflow" : false});
        }
    });
